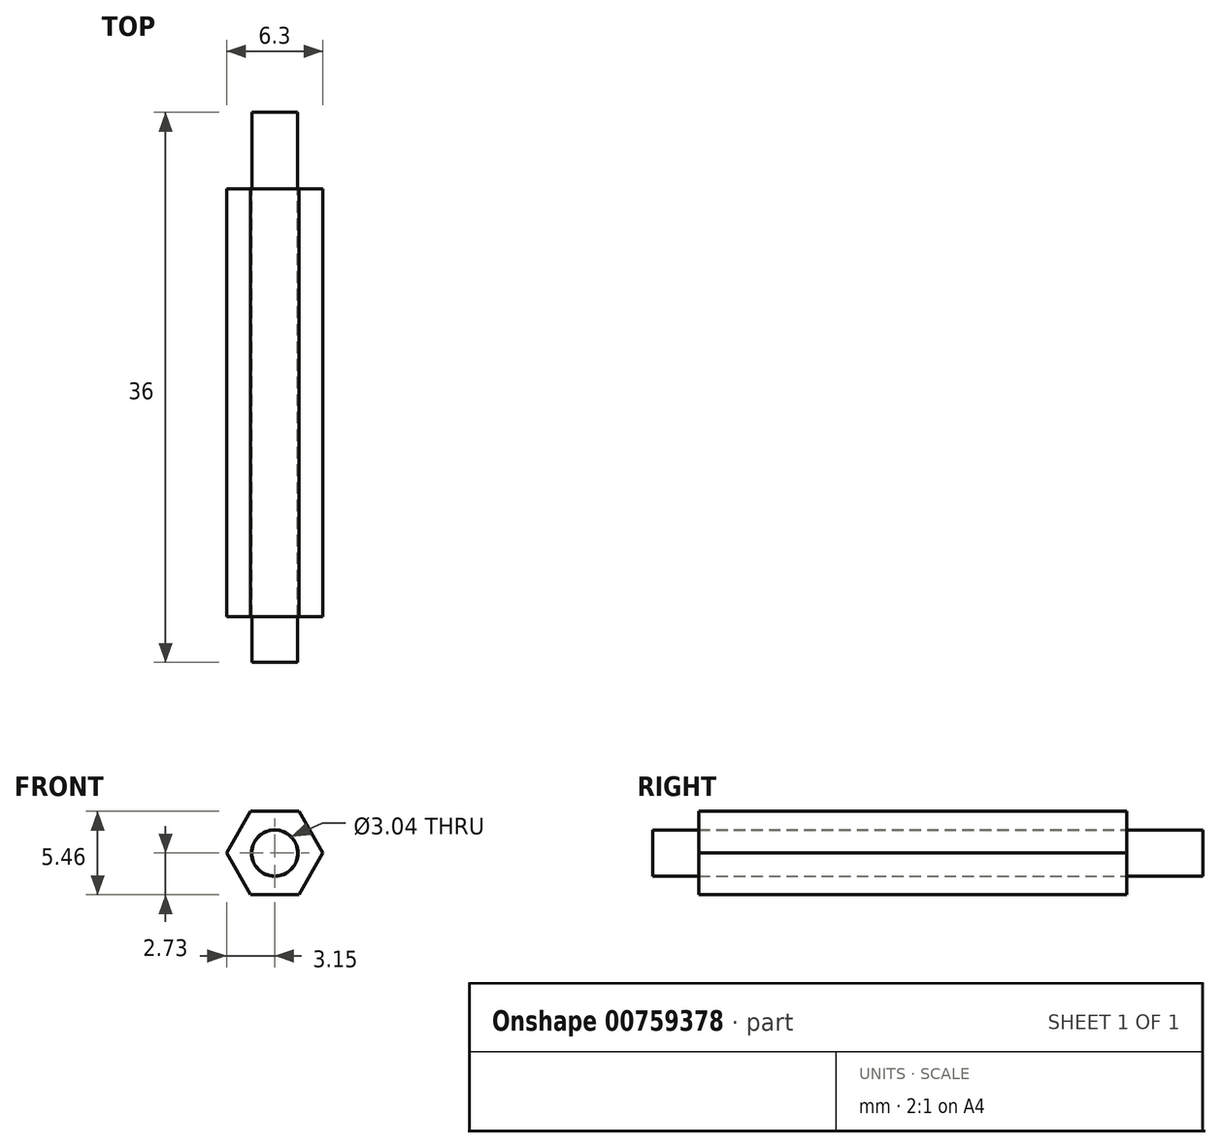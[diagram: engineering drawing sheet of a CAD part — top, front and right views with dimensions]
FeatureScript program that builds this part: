
annotation { "Feature Type Name" : "Feature", "Feature Type Description" : "" }
export const myFeature = defineFeature(function(context is Context, id is Id, definition is map)
    precondition{}
    {
        {
            var Q0;
            Q0=qCreatedBy(makeId("Front.planeOp"),FACE);
            var sketch = newSketch(context, id + "F0", { "sketchPlane" : qUnion([Q0])});
            skCircle(sketch, "E0.cCircle", {"center": v(0, 0) * mm, "radius": 2.73 * mm, "construction": true});
            skLineSegment(sketch, "E0.0", {"start": v(1.58, -2.73) * mm, "end": v(-1.58, -2.73) * mm});
            skLineSegment(sketch, "E0.1", {"start": v(-1.57, -2.73) * mm, "end": v(-3.15, 0) * mm});
            skLineSegment(sketch, "E0.2", {"start": v(-3.15, 0) * mm, "end": v(-1.57, 2.73) * mm});
            skLineSegment(sketch, "E0.3", {"start": v(-1.58, 2.73) * mm, "end": v(1.57, 2.73) * mm});
            skLineSegment(sketch, "E0.4", {"start": v(1.57, 2.73) * mm, "end": v(3.15, 0) * mm});
            skLineSegment(sketch, "E0.5", {"start": v(3.15, 0) * mm, "end": v(1.57, -2.73) * mm});
            skPoint(sketch, "E0.0.midPoint", {"position": v(0, -2.73) * mm});
            skCircle(sketch, "E1", {"center": v(0, 0) * mm, "radius": 1.5 * mm});
            skCircle(sketch, "E2", {"center": v(0, 0) * mm, "radius": 1.52 * mm});
            skSolve(sketch);
        }
        {
            var Q0;
            Q0=makeQuery(id+"F0.imprint","IMPRINT",FACE,{"disambiguationData":[TD([[makeQuery(id+"F0.imprint","IMPRINT",EDGE,{"derivedFrom":sQuery(id+"F0.wireOp",EDGE,"E0.0")}),-1.0]])]});
            var Q1;
            Q1=makeQuery(id+"F0.imprint","IMPRINT",FACE,{"disambiguationData":[TD([[makeQuery(id+"F0.imprint","IMPRINT",EDGE,{"derivedFrom":sQuery(id+"F0.wireOp",EDGE,"E1")}),1.0]])]});
            extrude(context, id + "F1", {"entities" : qUnion([Q0, Q1]), "depth" : 28 * mm, "offsetDistance" : 25 * mm});
        }
        {
            var Q0;
            Q0=makeQuery(id+"F0.imprint","IMPRINT",FACE,{"disambiguationData":[TD([[makeQuery(id+"F0.imprint","IMPRINT",EDGE,{"derivedFrom":sQuery(id+"F0.wireOp",EDGE,"E1")}),1.0]])]});
            extrude(context, id + "F2", {"entities" : qUnion([Q0]), "operationType" : NewBodyOperationType.ADD, "oppositeDirection" : true, "depth" : 5 * mm, "offsetDistance" : 25 * mm});
        }
        {
            var Q0;
            Q0=makeQuery(id+"F1.opExtrude","CAP_FACE",FACE,{"disambiguationData":[OSD([sQuery(id+"F0.wireOp",EDGE,"E1")])],"isStart":false});
            extrude(context, id + "F3", {"entities" : qUnion([Q0]), "operationType" : NewBodyOperationType.ADD, "depth" : 3 * mm, "offsetDistance" : 25 * mm});
        }
    });
